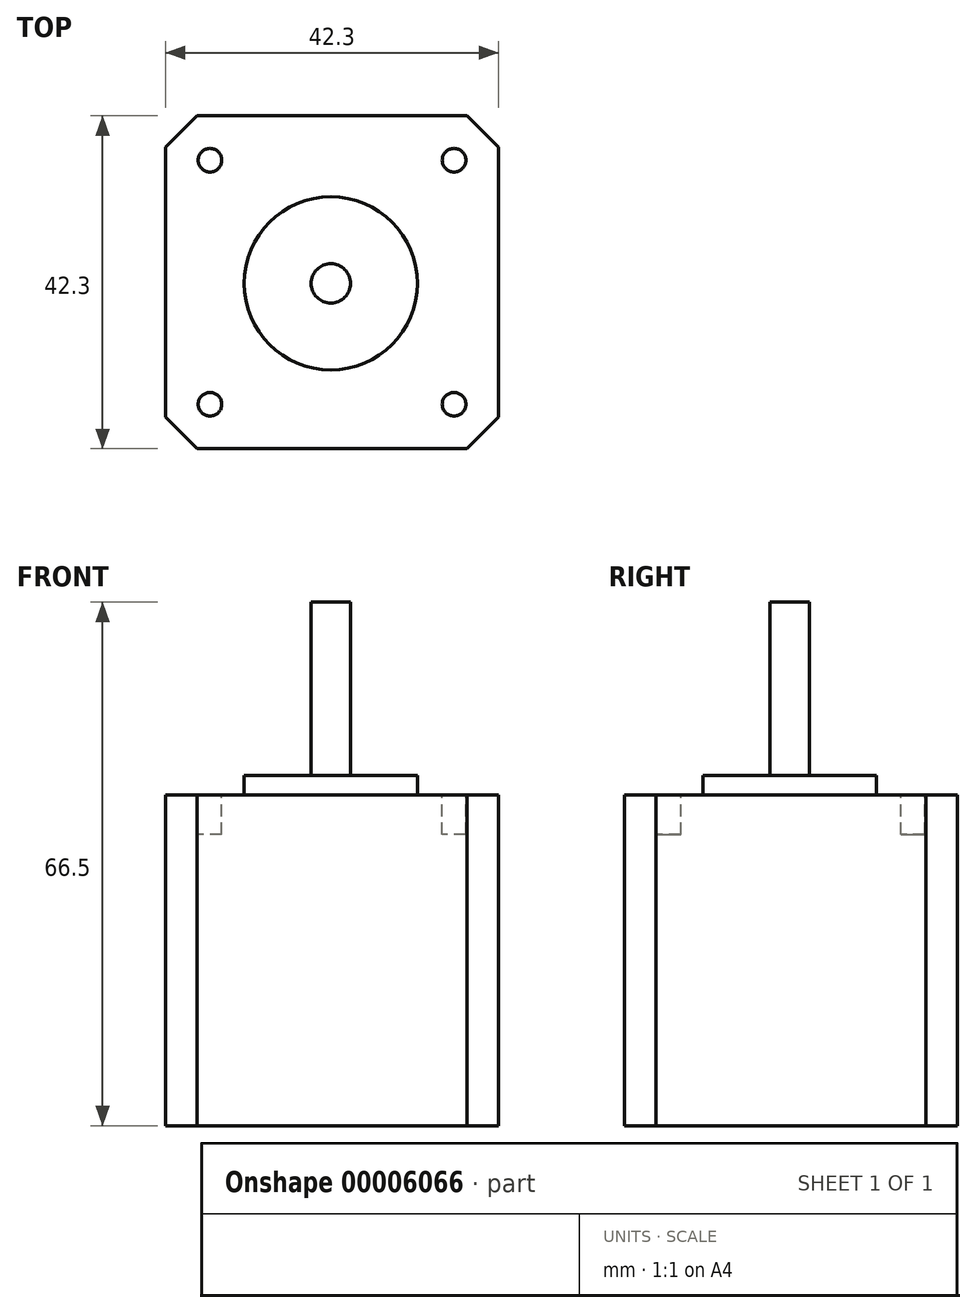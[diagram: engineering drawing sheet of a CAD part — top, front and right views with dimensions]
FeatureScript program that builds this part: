
annotation { "Feature Type Name" : "Feature", "Feature Type Description" : "" }
export const myFeature = defineFeature(function(context is Context, id is Id, definition is map)
    precondition{}
    {
        {
            var Q0;
            Q0=qCreatedBy(makeId("Top.planeOp"),FACE);
            var sketch = newSketch(context, id + "F0", { "sketchPlane" : qUnion([Q0])});
            skLineSegment(sketch, "E0.bottom", {"start": v(0, 0) * mm, "end": v(42.3, 0) * mm});
            skLineSegment(sketch, "E0.top", {"start": v(0, 42.3) * mm, "end": v(42.3, 42.3) * mm});
            skLineSegment(sketch, "E0.left", {"start": v(0, 0) * mm, "end": v(0, 42.3) * mm});
            skLineSegment(sketch, "E0.right", {"start": v(42.3, 0) * mm, "end": v(42.3, 42.3) * mm});
            skSolve(sketch);
        }
        {
            var Q0;
            Q0=qSketchRegion(id+"F0",true);
            extrude(context, id + "F1", {"entities" : qUnion([Q0]), "depth" : 42 * mm});
        }
        {
            var Q0;
            Q0=makeQuery(id+"F1.opExtrude","CAP_FACE",FACE,{"disambiguationData":[OSD([sQuery(id+"F0.wireOp",EDGE,"E0.bottom"),sQuery(id+"F0.wireOp",EDGE,"E0.top"),sQuery(id+"F0.wireOp",EDGE,"E0.left"),sQuery(id+"F0.wireOp",EDGE,"E0.right")])],"isStart":false});
            var sketch = newSketch(context, id + "F2", { "sketchPlane" : qUnion([Q0])});
            skLineSegment(sketch, "E1", {"start": v(0, 42.3) * mm, "end": v(42.3, 0) * mm, "construction": true});
            skLineSegment(sketch, "E2", {"start": v(0, 0) * mm, "end": v(42.3, 42.3) * mm, "construction": true});
            skLineSegment(sketch, "E3", {"start": v(5.65, 36.65) * mm, "end": v(36.65, 36.65) * mm, "construction": true});
            skLineSegment(sketch, "E4", {"start": v(36.65, 36.65) * mm, "end": v(36.65, 5.65) * mm, "construction": true});
            skLineSegment(sketch, "E5", {"start": v(36.65, 5.65) * mm, "end": v(5.65, 5.65) * mm, "construction": true});
            skLineSegment(sketch, "E6", {"start": v(5.65, 5.65) * mm, "end": v(5.65, 36.65) * mm, "construction": true});
            skCircle(sketch, "E7", {"center": v(5.65, 36.65) * mm, "radius": 1.5 * mm});
            skCircle(sketch, "E8", {"center": v(5.65, 5.65) * mm, "radius": 1.5 * mm});
            skCircle(sketch, "E9", {"center": v(36.65, 5.65) * mm, "radius": 1.5 * mm});
            skCircle(sketch, "E10", {"center": v(36.65, 36.65) * mm, "radius": 1.5 * mm});
            skSolve(sketch);
        }
        {
            var Q0;
            Q0=makeQuery(id+"F1.opExtrude","SWEPT_EDGE",EDGE,{"disambiguationData":[OSD([sQuery(id+"F0.wireOp",EDGE,"E0.bottom"),sQuery(id+"F0.wireOp",EDGE,"E0.left")])]});
            var Q1;
            Q1=makeQuery(id+"F1.opExtrude","SWEPT_EDGE",EDGE,{"disambiguationData":[OSD([sQuery(id+"F0.wireOp",EDGE,"E0.bottom"),sQuery(id+"F0.wireOp",EDGE,"E0.right")])]});
            var Q2;
            Q2=makeQuery(id+"F1.opExtrude","SWEPT_EDGE",EDGE,{"disambiguationData":[OSD([sQuery(id+"F0.wireOp",EDGE,"E0.top"),sQuery(id+"F0.wireOp",EDGE,"E0.right")])]});
            var Q3;
            Q3=makeQuery(id+"F1.opExtrude","SWEPT_EDGE",EDGE,{"disambiguationData":[OSD([sQuery(id+"F0.wireOp",EDGE,"E0.top"),sQuery(id+"F0.wireOp",EDGE,"E0.left")])]});
            chamfer(context, id + "F3", {"entities" : qUnion([Q0, Q1, Q2, Q3]), "width" : 4 * mm, "tangentPropagation" : true});
        }
        {
            var Q0;
            Q0=qSketchRegion(id+"F2",true);
            extrude(context, id + "F4", {"entities" : qUnion([Q0]), "operationType" : NewBodyOperationType.REMOVE, "oppositeDirection" : true, "depth" : 5 * mm});
        }
        {
            var Q0;
            Q0=makeQuery(id+"F1.opExtrude","CAP_FACE",FACE,{"disambiguationData":[OSD([sQuery(id+"F0.wireOp",EDGE,"E0.bottom"),sQuery(id+"F0.wireOp",EDGE,"E0.top"),sQuery(id+"F0.wireOp",EDGE,"E0.left"),sQuery(id+"F0.wireOp",EDGE,"E0.right")])],"isStart":false});
            var sketch = newSketch(context, id + "F5", { "sketchPlane" : qUnion([Q0])});
            skCircle(sketch, "E11", {"center": v(21, 21) * mm, "radius": 11 * mm});
            skSolve(sketch);
        }
        {
            var Q0;
            Q0=qSketchRegion(id+"F5",true);
            extrude(context, id + "F6", {"entities" : qUnion([Q0]), "operationType" : NewBodyOperationType.ADD, "depth" : 2.5 * mm});
        }
        {
            var Q0;
            Q0=makeQuery(id+"F6.opExtrude","CAP_FACE",FACE,{"disambiguationData":[OSD([sQuery(id+"F5.wireOp",EDGE,"E11")])],"isStart":false});
            var sketch = newSketch(context, id + "F7", { "sketchPlane" : qUnion([Q0])});
            skCircle(sketch, "E12", {"center": v(21, 21) * mm, "radius": 2.5 * mm});
            skSolve(sketch);
        }
        {
            var Q0;
            Q0=qSketchRegion(id+"F7",true);
            extrude(context, id + "F8", {"entities" : qUnion([Q0]), "operationType" : NewBodyOperationType.ADD, "depth" : 22 * mm});
        }
    });
